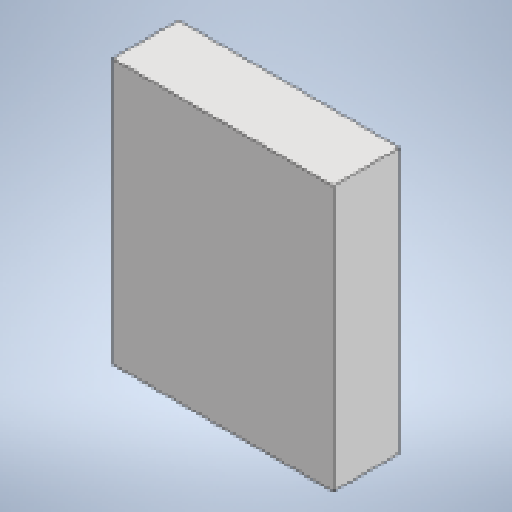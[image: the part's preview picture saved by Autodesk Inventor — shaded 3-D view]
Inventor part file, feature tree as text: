
AUTODESK INVENTOR PART (.ipt)
format: ipt  version: 2025.1 (Build 291241020, 241B)  size: 114,176 bytes
history: native  units: mm
features: extrude x1, sketch x1
ambient origin geometry x8: Origin, YZ Plane, XZ Plane, XY Plane, X Axis, Y Axis, Z Axis, Center Point
bodies: Solid1 (feature_tree)
feature tree (2):
  extrude  "Extrusion1"  Depth=300.0mm
  sketch  "Sketch1"  dims[d0=1000.0mm d1=300.0mm d2=1200.0mm d3=0.0mm]
